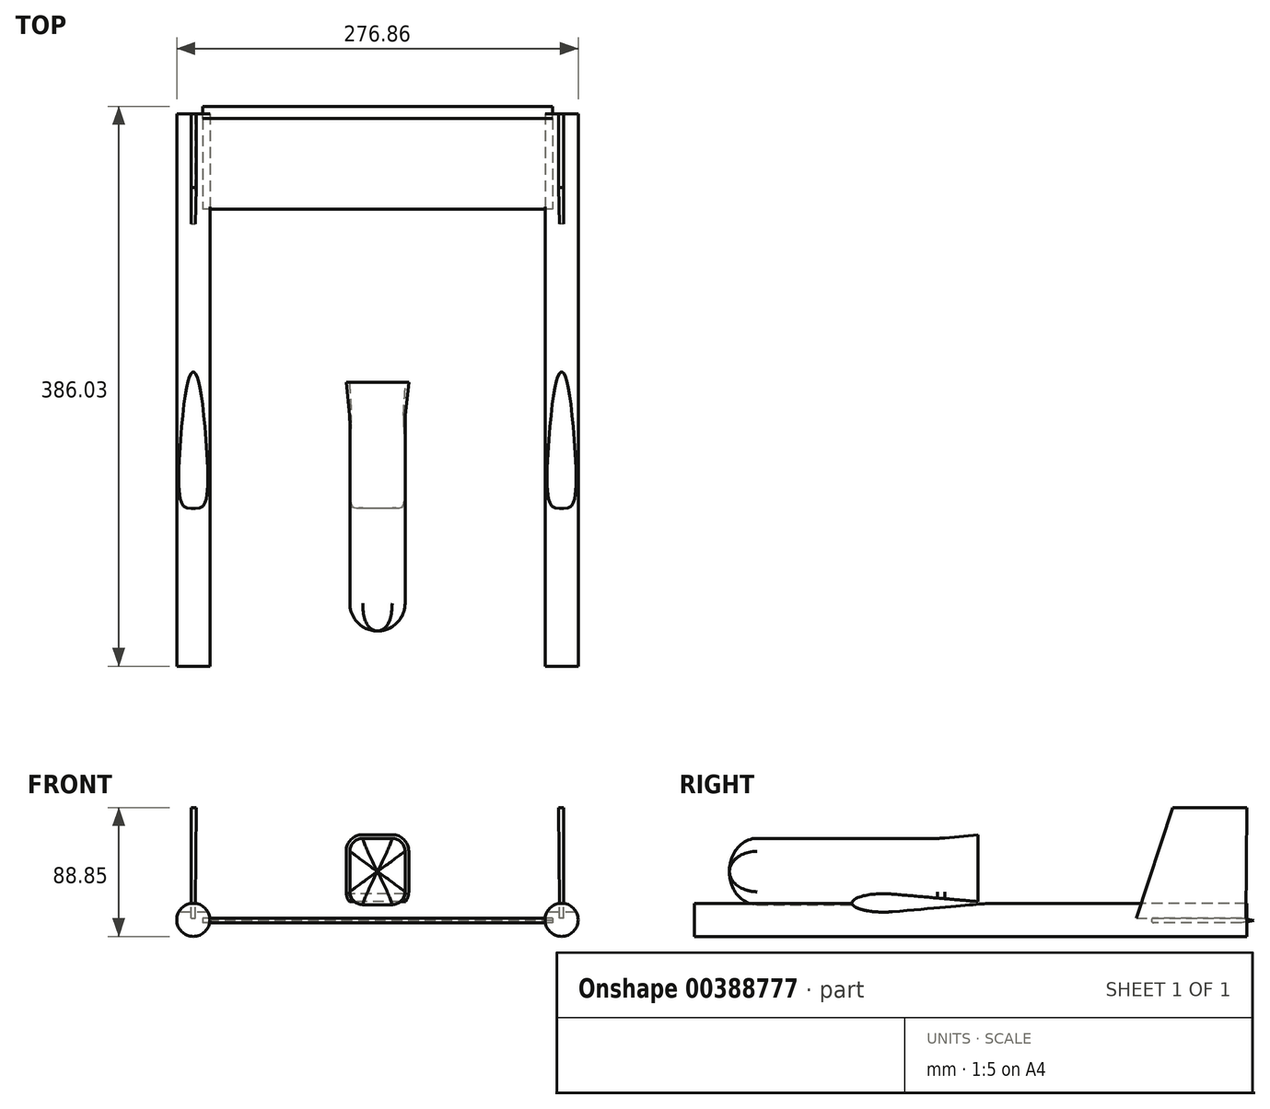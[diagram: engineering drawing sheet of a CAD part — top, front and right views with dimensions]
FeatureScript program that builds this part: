
annotation { "Feature Type Name" : "Feature", "Feature Type Description" : "" }
export const myFeature = defineFeature(function(context is Context, id is Id, definition is map)
    precondition{}
    {
        {
            var Q0;
            Q0=qCreatedBy(makeId("Right.planeOp"),FACE);
            var sketch = newSketch(context, id + "F0", { "sketchPlane" : qUnion([Q0])});
            skLineSegment(sketch, "E0.bottom", {"start": v(-58.28, 29.27) * mm, "end": v(68.72, 29.27) * mm});
            skLineSegment(sketch, "E0.top", {"start": v(-58.28, -16.45) * mm, "end": v(68.72, -16.45) * mm});
            skLineSegment(sketch, "E0.right", {"start": v(68.72, 29.27) * mm, "end": v(68.72, -16.45) * mm});
            skEllipticalArc(sketch, "E1", {});
            const initialGuessF0  = {"E1": [-0.058275784969329836, 0.006413180471062662, 0, -1, 0.02286, 0.01903408044552587, 3.141592653589793, 0]};
            skSetInitialGuess(sketch, initialGuessF0);
            skSolve(sketch);
        }
        {
            var Q0;
            Q0 = qSketchRegion(id + "F0", true);
            extrude(context, id + "F1", {"entities" : qUnion([Q0]), "endBound" : BoundingType.SYMMETRIC, "depth" : 38.1 * mm});
        }
        {
            var Q0;
            Q0=makeQuery(id+"F1.opExtrude","CAP_EDGE",EDGE,{"disambiguationData":[OSD([sQuery(id+"F0.wireOp",EDGE,"E0.bottom")])],"isStart":false});
            var Q1;
            Q1=makeQuery(id+"F1.opExtrude","CAP_EDGE",EDGE,{"disambiguationData":[OSD([sQuery(id+"F0.wireOp",EDGE,"E0.bottom")])],"isStart":true});
            var Q2;
            Q2=makeQuery(id+"F1.opExtrude","CAP_EDGE",EDGE,{"disambiguationData":[OSD([sQuery(id+"F0.wireOp",EDGE,"E0.top")])],"isStart":false});
            var Q3;
            Q3=makeQuery(id+"F1.opExtrude","CAP_EDGE",EDGE,{"disambiguationData":[OSD([sQuery(id+"F0.wireOp",EDGE,"E0.top")])],"isStart":true});
            fillet(context, id + "F2", {"entities" : qUnion([Q0, Q1, Q2, Q3]), "radius" : 5.08 * mm, "tangentPropagation" : true, "allowEdgeOverflow" : false});
        }
        {
            var Q0;
            Q0=makeQuery(id+"F1.opExtrude","SWEPT_FACE",FACE,{"disambiguationData":[OSD([sQuery(id+"F0.wireOp",EDGE,"E0.bottom")])]});
            var sketch = newSketch(context, id + "F3", { "sketchPlane" : qUnion([Q0])});
            skEllipticalArc(sketch, "E2", {});
            skLineSegment(sketch, "E3.0", {"start": v(13.97, -58.28) * mm, "end": v(-13.97, -58.28) * mm});
            skLineSegment(sketch, "E4", {"start": v(-19.05, -58.28) * mm, "end": v(-20.85, -58.28) * mm});
            skLineSegment(sketch, "E5", {"start": v(-20.85, -58.28) * mm, "end": v(-20.85, -82.51) * mm});
            skLineSegment(sketch, "E6", {"start": v(-20.85, -82.51) * mm, "end": v(22, -82.51) * mm});
            skLineSegment(sketch, "E7", {"start": v(22, -82.51) * mm, "end": v(22, -58.28) * mm});
            skLineSegment(sketch, "E8", {"start": v(22, -58.28) * mm, "end": v(19.05, -58.28) * mm});
            const initialGuessF3  = {"E2": [0, -0.058275784969329836, 1, 0, 0.01905, 0.01903408044552587, 3.141592653589793, 0]};
            skSetInitialGuess(sketch, initialGuessF3);
            skSolve(sketch);
        }
        {
            var Q0;
            Q0 = qSketchRegion(id + "F3", true);
            var Q1;
            Q1=makeQuery(id+"F1.opExtrude","SWEPT_FACE",FACE,{"disambiguationData":[OSD([sQuery(id+"F0.wireOp",EDGE,"E0.top")])]});
            extrude(context, id + "F4", {"entities" : qUnion([Q0]), "operationType" : NewBodyOperationType.REMOVE, "endBound" : BoundingType.UP_TO_SURFACE, "oppositeDirection" : true, "endBoundEntityFace" : qUnion([Q1]), "depth" : 25.4 * mm});
        }
        {
            var Q0;
            Q0=makeQuery(id+"F4.boolean.opBoolean","INTERSECT",EDGE,{"disambiguationData":[OD(1.0)],"derivedFrom":[makeQuery(id+"F1.opExtrude","SWEPT_FACE",FACE,{"disambiguationData":[OSD([sQuery(id+"F0.wireOp",EDGE,"E1")])]}),makeQuery(id+"F4.opExtrude","SWEPT_FACE",FACE,{"disambiguationData":[OSD([sQuery(id+"F3.wireOp",EDGE,"E2")])]})]});
            var Q1;
            Q1=makeQuery(id+"F4.boolean.opBoolean","INTERSECT",EDGE,{"disambiguationData":[OD(2.0)],"derivedFrom":[makeQuery(id+"F1.opExtrude","SWEPT_FACE",FACE,{"disambiguationData":[OSD([sQuery(id+"F0.wireOp",EDGE,"E1")])]}),makeQuery(id+"F4.opExtrude","SWEPT_FACE",FACE,{"disambiguationData":[OSD([sQuery(id+"F3.wireOp",EDGE,"E2")])]})]});
            var Q2;
            Q2=makeQuery(id+"F4.boolean.opBoolean","INTERSECT",EDGE,{"disambiguationData":[OD(3.0)],"derivedFrom":[makeQuery(id+"F1.opExtrude","SWEPT_FACE",FACE,{"disambiguationData":[OSD([sQuery(id+"F0.wireOp",EDGE,"E1")])]}),makeQuery(id+"F4.opExtrude","SWEPT_FACE",FACE,{"disambiguationData":[OSD([sQuery(id+"F3.wireOp",EDGE,"E2")])]})]});
            var Q3;
            Q3=makeQuery(id+"F4.boolean.opBoolean","INTERSECT",EDGE,{"disambiguationData":[OD(0.0)],"derivedFrom":[makeQuery(id+"F1.opExtrude","SWEPT_FACE",FACE,{"disambiguationData":[OSD([sQuery(id+"F0.wireOp",EDGE,"E1")])]}),makeQuery(id+"F4.opExtrude","SWEPT_FACE",FACE,{"disambiguationData":[OSD([sQuery(id+"F3.wireOp",EDGE,"E2")])]})]});
            fillet(context, id + "F5", {"entities" : qUnion([Q0, Q1, Q2, Q3]), "radius" : 8.9 * mm, "tangentPropagation" : true, "allowEdgeOverflow" : false});
        }
        {
            var Q0;
            Q0=qCreatedBy(makeId("Right.planeOp"),FACE);
            var sketch = newSketch(context, id + "F6", { "sketchPlane" : qUnion([Q0])});
            skEllipse(sketch, "E9", {"center": v(28.8, -15.25) * mm, "majorRadius": 21.59 * mm, "minorRadius": 6.35 * mm, "majorAxis": v(1, 0)});
            skLineSegment(sketch, "E10", {"start": v(29.86, -8.72) * mm, "end": v(104.63, -15.25) * mm});
            skLineSegment(sketch, "E11", {"start": v(104.63, -15.25) * mm, "end": v(34.96, -21.34) * mm});
            skSolve(sketch);
        }
        {
            var Q0;
            Q0 = qSketchRegion(id + "F6", true);
            extrude(context, id + "F7", {"entities" : qUnion([Q0]), "operationType" : NewBodyOperationType.REMOVE, "endBound" : BoundingType.SYMMETRIC, "oppositeDirection" : true, "depth" : 101.6 * mm});
        }
        {
            var Q0;
            Q0 = qSketchRegion(id + "F6", true);
            extrude(context, id + "F8", {"entities" : qUnion([Q0]), "endBound" : BoundingType.SYMMETRIC, "depth" : 762 * mm});
        }
        {
            var Q0;
            Q0=qCreatedBy(makeId("Front.planeOp"),FACE);
            var sketch = newSketch(context, id + "F9", { "sketchPlane" : qUnion([Q0])});
            skCircle(sketch, "E12", {"center": v(-127, -26.94) * mm, "radius": 11.43 * mm});
            skCircle(sketch, "E13.MirrorC", {"center": v(127, -26.94) * mm, "radius": 11.43 * mm});
            skSolve(sketch);
        }
        {
            var Q0;
            Q0 = qSketchRegion(id + "F9", true);
            extrude(context, id + "F10", {"entities" : qUnion([Q0]), "operationType" : NewBodyOperationType.REMOVE, "oppositeDirection" : true, "depth" : 127 * mm});
        }
        {
            var Q0;
            Q0 = qSketchRegion(id + "F9", true);
            extrude(context, id + "F11", {"entities" : qUnion([Q0]), "oppositeDirection" : true, "depth" : 279.4 * mm, "hasSecondDirection" : true, "secondDirectionOppositeDirection" : false, "secondDirectionDepth" : 101.6 * mm});
        }
        {
            var Q0;
            Q0=qCreatedBy(makeId("Right.planeOp"),FACE);
            var sketch = newSketch(context, id + "F12", { "sketchPlane" : qUnion([Q0])});
            skLineSegment(sketch, "E14.bottom", {"start": v(276, -25.72) * mm, "end": v(215.24, -25.72) * mm});
            skLineSegment(sketch, "E14.top", {"start": v(276, -28.86) * mm, "end": v(215.24, -28.86) * mm});
            skLineSegment(sketch, "E14.left", {"start": v(276, -25.72) * mm, "end": v(276, -28.86) * mm});
            skLineSegment(sketch, "E14.right", {"start": v(215.24, -25.72) * mm, "end": v(215.24, -28.86) * mm});
            skLineSegment(sketch, "E15", {"start": v(276, -25.72) * mm, "end": v(284.43, -27.3) * mm});
            skLineSegment(sketch, "E16", {"start": v(284.43, -27.3) * mm, "end": v(276, -28.86) * mm});
            skCircle(sketch, "E17", {"center": v(215.24, -27.3) * mm, "radius": 1.57 * mm});
            skSolve(sketch);
        }
        {
            var Q0;
            Q0 = qSketchRegion(id + "F12", true);
            extrude(context, id + "F13", {"entities" : qUnion([Q0]), "endBound" : BoundingType.SYMMETRIC, "depth" : 241.3 * mm});
        }
        {
            var Q0;
            Q0=qCreatedBy(makeId("Front.planeOp"),FACE);
            var sketch = newSketch(context, id + "F14", { "sketchPlane" : qUnion([Q0])});
            skLineSegment(sketch, "E18", {"start": v(-368.83, -21.34) * mm, "end": v(-381, -9.17) * mm});
            skLineSegment(sketch, "E19", {"start": v(-381, -9.17) * mm, "end": v(-381, -21.34) * mm});
            skLineSegment(sketch, "E20", {"start": v(-381, -21.34) * mm, "end": v(-368.83, -21.34) * mm});
            skLineSegment(sketch, "E21.MirrorCS", {"start": v(381, -9.17) * mm, "end": v(381, -21.34) * mm});
            skLineSegment(sketch, "E22.MirrorCS", {"start": v(381, -21.34) * mm, "end": v(368.83, -21.34) * mm});
            skLineSegment(sketch, "E23.MirrorCS", {"start": v(368.83, -21.34) * mm, "end": v(381, -9.17) * mm});
            skLineSegment(sketch, "E24.bottom", {"start": v(-381, -21.34) * mm, "end": v(-368.33, -21.34) * mm});
            skLineSegment(sketch, "E24.top", {"start": v(-381, -27.22) * mm, "end": v(-368.33, -27.22) * mm});
            skLineSegment(sketch, "E24.left", {"start": v(-381, -21.34) * mm, "end": v(-381, -27.22) * mm});
            skLineSegment(sketch, "E24.right", {"start": v(-368.33, -21.34) * mm, "end": v(-368.33, -27.22) * mm});
            skLineSegment(sketch, "E25.MirrorCS", {"start": v(381, -21.34) * mm, "end": v(381, -27.22) * mm});
            skLineSegment(sketch, "E26.MirrorCS", {"start": v(368.33, -21.34) * mm, "end": v(368.33, -27.22) * mm});
            skLineSegment(sketch, "E27.MirrorCS", {"start": v(381, -27.22) * mm, "end": v(368.33, -27.22) * mm});
            skSolve(sketch);
        }
        {
            var Q0;
            Q0 = qSketchRegion(id + "F14", true);
            extrude(context, id + "F15", {"entities" : qUnion([Q0]), "operationType" : NewBodyOperationType.REMOVE, "oppositeDirection" : true, "depth" : 254 * mm});
        }
        {
            var Q0;
            Q0=makeQuery(id+"F15.boolean.opBoolean","COPY",FACE,{"derivedFrom":makeQuery(id+"F15.opExtrude","SWEPT_FACE",FACE,{"disambiguationData":[OSD([sQuery(id+"F14.wireOp",EDGE,"E23.MirrorCS")])]})});
            extrude(context, id + "F16", {"entities" : qUnion([Q0]), "operationType" : NewBodyOperationType.REMOVE, "depth" : 25.4 * mm});
        }
        {
            var Q0;
            Q0=makeQuery(id+"F1.opExtrude","SWEPT_FACE",FACE,{"disambiguationData":[OSD([sQuery(id+"F0.wireOp",EDGE,"E0.right")])]});
            cPlane(context, id + "F17", {"entities" : qUnion([Q0]), "cplaneType" : CPlaneType.OFFSET, "offset" : 25.4 * mm, "width" : 152.4 * mm, "height" : 152.4 * mm});
        }
        {
            var Q0;
            Q0=qCreatedBy(id+"F17.planeOp",FACE);
            var sketch = newSketch(context, id + "F18", { "sketchPlane" : qUnion([Q0])});
            skLineSegment(sketch, "E28.0", {"start": v(-21.59, 20.38) * mm, "end": v(-21.59, -7.56) * mm});
            skArc(sketch, "E28.1", {"start": v(-10.16, 31.81) * mm, "mid": v(-18.24, 28.47) * mm, "end": v(-21.59, 20.38) * mm});
            skArc(sketch, "E28.2", {"start": v(-21.59, -7.56) * mm, "mid": v(-20.95, -11.32) * mm, "end": v(-19.12, -14.66) * mm});
            skLineSegment(sketch, "E28.3", {"start": v(10.16, 31.81) * mm, "end": v(-10.16, 31.81) * mm});
            skLineSegment(sketch, "E28.4", {"start": v(-19.12, -14.66) * mm, "end": v(19.12, -14.66) * mm});
            skArc(sketch, "E28.5", {"start": v(19.12, -14.66) * mm, "mid": v(20.95, -11.32) * mm, "end": v(21.59, -7.56) * mm});
            skLineSegment(sketch, "E28.6", {"start": v(21.59, -7.56) * mm, "end": v(21.59, 20.38) * mm});
            skArc(sketch, "E28.7", {"start": v(21.59, 20.38) * mm, "mid": v(18.24, 28.47) * mm, "end": v(10.16, 31.81) * mm});
            skSolve(sketch);
        }
        {
            var Q1;
            Q1=makeQuery(id+"F18.imprint","IMPRINT",FACE,{"disambiguationData":[TD([[makeQuery(id+"F18.imprint","IMPRINT",EDGE,{"derivedFrom":sQuery(id+"F18.wireOp",EDGE,"E28.0")}),1.0]])]});
            var Q2;
            Q2=makeQuery(id+"F1.opExtrude","SWEPT_FACE",FACE,{"disambiguationData":[OSD([sQuery(id+"F0.wireOp",EDGE,"E0.right")])]});
            loft(context, id + "F19", {"operationType" : NewBodyOperationType.ADD, "sheetProfilesArray" : [{ "sheetProfileEntities" : qUnion([Q1]) }, { "sheetProfileEntities" : qUnion([Q2]) }]});
        }
        {
            var Q0;
            {var subQ0=sQuery(id+"F0.wireOp",EDGE,"E0.right");var subQ1=makeQuery(id+"F1.opExtrude","CAP_EDGE",EDGE,{"disambiguationData":[OSD([subQ0])],"isStart":false});var subQ2=sQuery(id+"F0.wireOp",EDGE,"E1");var subQ3=sQuery(id+"F0.wireOp",EDGE,"E0.top");var subQ4=sQuery(id+"F0.wireOp",EDGE,"E0.bottom");var subQ5=makeQuery(id+"F1.opExtrude","CAP_FACE",FACE,{"disambiguationData":[OSD([subQ4,subQ3,subQ0,subQ2])],"isStart":false});var subQ6=makeQuery(id+"F1.opExtrude","SWEPT_FACE",FACE,{"disambiguationData":[OSD([subQ0])]});var subQ7=sQuery(id+"F3.wireOp",EDGE,"E2");var subQ8=makeQuery(id+"F4.opExtrude","SWEPT_FACE",FACE,{"disambiguationData":[OSD([subQ7])]});var subQ9=makeQuery(id+"F1.opExtrude","SWEPT_FACE",FACE,{"disambiguationData":[OSD([subQ2])]});Q0=makeQuery(id+"F19.boolean.opBoolean","MERGE",EDGE,{"derivedFrom":[subQ1,makeQuery(id+"F19.opLoft","MID_CAP_EDGE",EDGE,{"disambiguationData":[OSD([subQ4,subQ3,subQ0,subQ2,subQ7]),TDD([makeQuery(id+"F5.opFillet","BLEND_VERTEX",VERTEX,{"blendedFrom":[makeQuery(id+"F4.boolean.opBoolean","INTERSECT",EDGE,{"disambiguationData":[OD(1.0)],"derivedFrom":[subQ9,subQ8]}),subQ6,subQ5],"blendedInto":[subQ6,subQ5]}),makeQuery(id+"F5.opFillet","BLEND_VERTEX",VERTEX,{"blendedFrom":[makeQuery(id+"F4.boolean.opBoolean","INTERSECT",EDGE,{"disambiguationData":[OD(3.0)],"derivedFrom":[subQ9,subQ8]}),subQ6,subQ5],"blendedInto":[subQ6,subQ5]}),subQ1])],"capPos":1.0})]});}
            fillet(context, id + "F20", {"entities" : qUnion([Q0]), "radius" : 50.8 * mm, "tangentPropagation" : true, "allowEdgeOverflow" : false});
        }
        {
            var Q0;
            Q0=qCreatedBy(makeId("Right.planeOp"),FACE);
            var sketch = newSketch(context, id + "F21", { "sketchPlane" : qUnion([Q0])});
            skLineSegment(sketch, "E29.0", {"start": v(29.86, -8.72) * mm, "end": v(104.63, -15.25) * mm});
            skLineSegment(sketch, "E30.0", {"start": v(104.63, -15.25) * mm, "end": v(34.96, -21.34) * mm});
            skEllipticalArc(sketch, "E31.0", {});
            const initialGuessF21  = {"E31.0": [0.02880894603032102, -0.015252540819346901, 1, 0, 0.02159, 0.00635, 1.2820698926992773, 5.001115414480309]};
            skSetInitialGuess(sketch, initialGuessF21);
            skSolve(sketch);
        }
        {
            var Q0;
            Q0 = qSketchRegion(id + "F21", true);
            extrude(context, id + "F22", {"entities" : qUnion([Q0]), "operationType" : NewBodyOperationType.REMOVE, "endBound" : BoundingType.SYMMETRIC, "depth" : 762 * mm});
        }
        {
            var Q0;
            Q0=makeQuery(id+"F13.opExtrude","SWEPT_FACE",FACE,{"disambiguationData":[OSD([sQuery(id+"F12.wireOp",EDGE,"E14.bottom")])]});
            var sketch = newSketch(context, id + "F23", { "sketchPlane" : qUnion([Q0])});
            skLineSegment(sketch, "E32.bottom", {"start": v(128.51, 203.27) * mm, "end": v(125.56, 203.27) * mm});
            skLineSegment(sketch, "E32.top", {"start": v(128.51, 278.84) * mm, "end": v(125.56, 278.84) * mm});
            skLineSegment(sketch, "E32.left", {"start": v(128.51, 203.27) * mm, "end": v(128.51, 278.84) * mm});
            skLineSegment(sketch, "E32.right", {"start": v(125.56, 203.27) * mm, "end": v(125.56, 278.84) * mm});
            skSolve(sketch);
        }
        {
            var Q0;
            {var subQ0=sQuery(id+"F12.wireOp",EDGE,"E14.bottom");Q0=makeQuery(id+"F23.imprint","IMPRINT",FACE,{"disambiguationData":[TD([[makeQuery(id+"F23.imprint","IMPRINT",EDGE,{"derivedFrom":makeQuery(id+"F13.opExtrude","CAP_EDGE",EDGE,{"disambiguationData":[OSD([subQ0])],"isStart":true})}),1.0]])]});}
            cPlane(context, id + "F24", {"entities" : qUnion([Q0]), "cplaneType" : CPlaneType.OFFSET, "offset" : 76.2 * mm, "width" : 152.4 * mm, "height" : 152.4 * mm});
        }
        {
            var Q0;
            Q0=qCreatedBy(id+"F24.planeOp",FACE);
            var sketch = newSketch(context, id + "F25", { "sketchPlane" : qUnion([Q0])});
            skLineSegment(sketch, "E33.bottom", {"start": v(124.83, 279.4) * mm, "end": v(128.51, 279.4) * mm});
            skLineSegment(sketch, "E33.top", {"start": v(124.83, 228.6) * mm, "end": v(128.51, 228.6) * mm});
            skLineSegment(sketch, "E33.left", {"start": v(124.83, 279.4) * mm, "end": v(124.83, 228.6) * mm});
            skLineSegment(sketch, "E33.right", {"start": v(128.51, 279.4) * mm, "end": v(128.51, 228.6) * mm});
            skSolve(sketch);
        }
        {
            var Q1;
            Q1 = qSketchRegion(id + "F23", true);
            var Q2;
            Q2 = qSketchRegion(id + "F25", true);
            loft(context, id + "F26", {"sheetProfilesArray" : [{ "sheetProfileEntities" : qUnion([Q1]) }, { "sheetProfileEntities" : qUnion([Q2]) }]});
        }
        {
            var Q0;
            Q0=makeQuery(id+"F26.opLoft","SWEPT_BODY",BODY,{"disambiguationData":[OSD([makeQuery(id+"F23.imprint","IMPRINT",FACE,{"disambiguationData":[TD([[makeQuery(id+"F23.imprint","IMPRINT",EDGE,{"derivedFrom":sQuery(id+"F23.wireOp",EDGE,"E32.bottom")}),-1.0]])]}),makeQuery(id+"F25.imprint","IMPRINT",FACE,{"disambiguationData":[TD([[makeQuery(id+"F25.imprint","IMPRINT",EDGE,{"derivedFrom":sQuery(id+"F25.wireOp",EDGE,"E33.bottom")}),-1.0]])]})])]});
            var Q1;
            Q1=qCreatedBy(makeId("Right.planeOp"),FACE);
            mirror(context, id + "F27", {"entities" : qUnion([Q0]), "mirrorPlane" : qUnion([Q1])});
        }
    });
